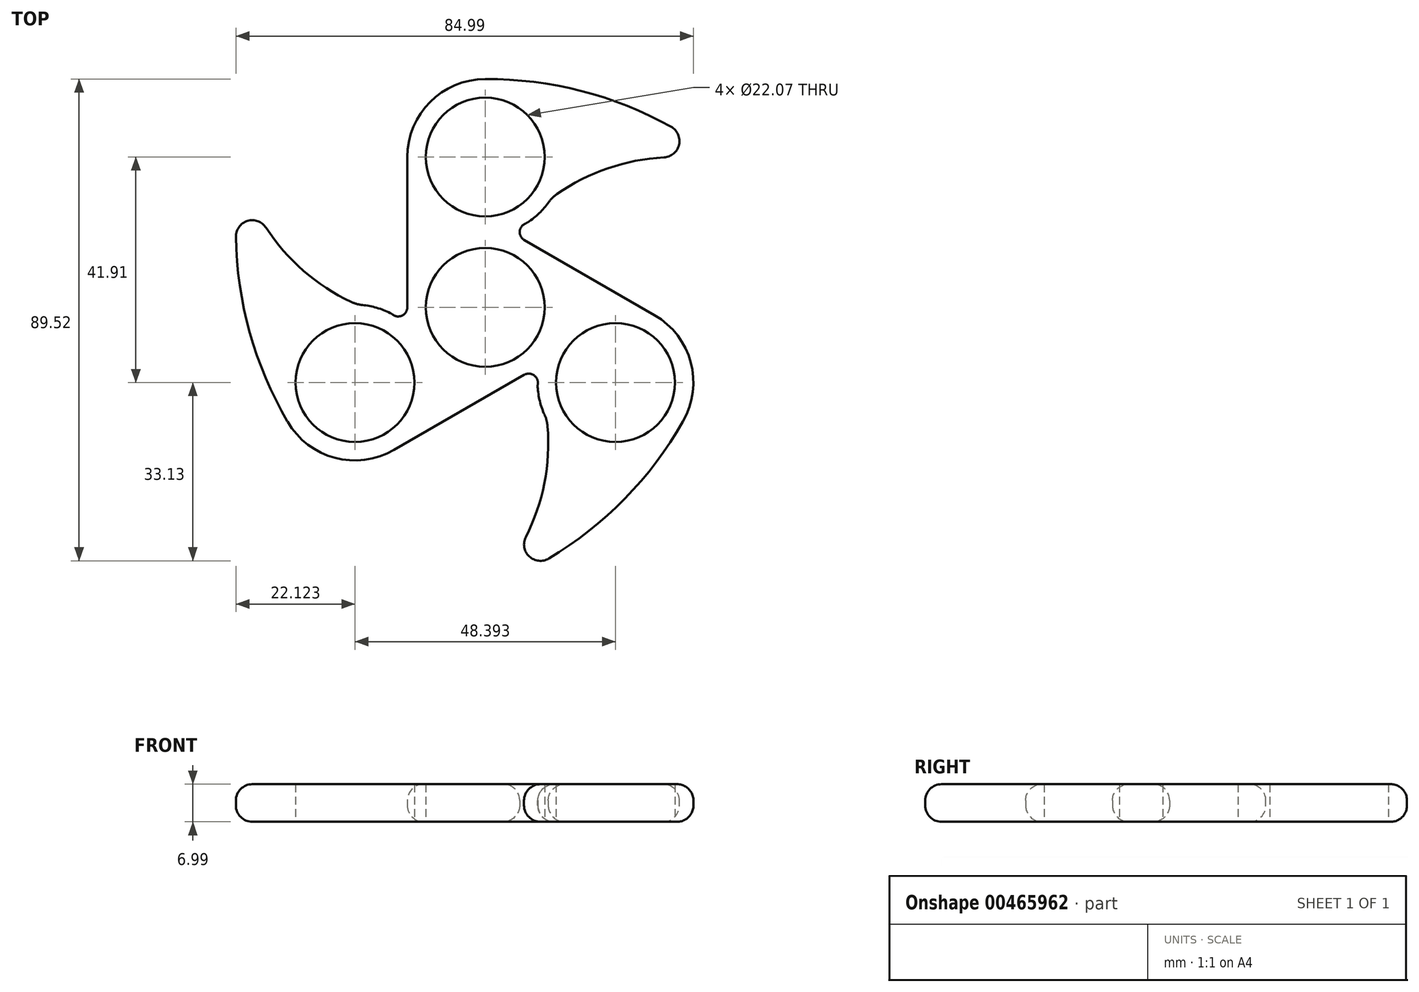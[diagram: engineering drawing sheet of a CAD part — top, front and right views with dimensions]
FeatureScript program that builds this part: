
annotation { "Feature Type Name" : "Feature", "Feature Type Description" : "" }
export const myFeature = defineFeature(function(context is Context, id is Id, definition is map)
    precondition{}
    {
        {
            var Q0;
            Q0=qCreatedBy(makeId("Top.planeOp"),FACE);
            var sketch = newSketch(context, id + "F0", { "sketchPlane" : qUnion([Q0])});
            skCircle(sketch, "E0", {"center": v(0, 0) * mm, "radius": 11.04 * mm});
            skCircle(sketch, "E1", {"center": v(0, 27.94) * mm, "radius": 11.04 * mm});
            skCircle(sketch, "E2.1.0", {"center": v(-24.2, -13.97) * mm, "radius": 11.04 * mm});
            skCircle(sketch, "E2.2.0", {"center": v(24.2, -13.97) * mm, "radius": 11.04 * mm});
            skCircle(sketch, "E3", {"center": v(0, 27.94) * mm, "radius": 12.7 * mm});
            skCircle(sketch, "E4", {"center": v(-24.2, -13.97) * mm, "radius": 12.7 * mm});
            skCircle(sketch, "E5", {"center": v(0, 0) * mm, "radius": 12.7 * mm});
            skCircle(sketch, "E6", {"center": v(24.2, -13.97) * mm, "radius": 12.7 * mm});
            skLineSegment(sketch, "E7", {"start": v(0, 27.94) * mm, "end": v(-12.7, 27.94) * mm});
            skLineSegment(sketch, "E8", {"start": v(0, 0) * mm, "end": v(-12.7, 0) * mm});
            skLineSegment(sketch, "E9", {"start": v(-14.47, 27.94) * mm, "end": v(-14.47, 0) * mm});
            skLineSegment(sketch, "E10.2.1", {"start": v(31.43, -1.43) * mm, "end": v(7.24, 12.54) * mm});
            skArc(sketch, "E11", {"start": v(11.78, 19.53) * mm, "mid": v(9.9, 17.37) * mm, "end": v(7.61, 15.63) * mm});
            skArc(sketch, "E12", {"start": v(7.61, 15.63) * mm, "mid": v(6.4, 14.2) * mm, "end": v(7.24, 12.54) * mm});
            skLineSegment(sketch, "E13.1.0", {"start": v(-16.96, -26.5) * mm, "end": v(7.24, -12.54) * mm});
            skArc(sketch, "E13.1.1", {"start": v(-16.96, -26.5) * mm, "mid": v(-38.67, -14.19) * mm, "end": v(-17.34, -1.22) * mm});
            skArc(sketch, "E13.1.2", {"start": v(-17.34, -1.22) * mm, "mid": v(-15.5, -1.56) * mm, "end": v(-14.47, 0) * mm});
            skArc(sketch, "E13.2.1", {"start": v(31.43, -1.43) * mm, "mid": v(31.62, -26.4) * mm, "end": v(9.73, -14.4) * mm});
            skArc(sketch, "E13.2.2", {"start": v(9.73, -14.4) * mm, "mid": v(9.1, -12.65) * mm, "end": v(7.24, -12.54) * mm});
            skLineSegment(sketch, "E14", {"start": v(0, 27.94) * mm, "end": v(0, 42.41) * mm});
            skArc(sketch, "E15", {"start": v(44.57, 26.77) * mm, "mid": v(23.64, 38.45) * mm, "end": v(0, 42.41) * mm});
            skArc(sketch, "E16", {"start": v(44.57, 26.77) * mm, "mid": v(28.33, 27.3) * mm, "end": v(13.33, 21.06) * mm});
            skPoint(sketch, "E17.newPointB", {"position": v(-14.47, 27.94) * mm});
            skArc(sketch, "E17.filletArc", {"start": v(13.33, 21.06) * mm, "mid": v(12.5, 20.36) * mm, "end": v(11.78, 19.53) * mm});
            skArc(sketch, "E18", {"start": v(0, 42.41) * mm, "mid": v(-10.24, 38.18) * mm, "end": v(-14.47, 27.94) * mm});
            skArc(sketch, "E19.1.0", {"start": v(-45.47, 25.21) * mm, "mid": v(-45.12, 1.25) * mm, "end": v(-36.73, -21.2) * mm});
            skArc(sketch, "E19.1.1", {"start": v(-45.47, 25.21) * mm, "mid": v(-37.8, 10.9) * mm, "end": v(-24.9, 1.02) * mm});
            skArc(sketch, "E19.1.2", {"start": v(-22.8, 0.44) * mm, "mid": v(-20, -0.12) * mm, "end": v(-17.34, -1.22) * mm});
            skArc(sketch, "E19.1.3", {"start": v(-24.9, 1.02) * mm, "mid": v(-23.88, 0.64) * mm, "end": v(-22.8, 0.44) * mm});
            skArc(sketch, "E19.2.0", {"start": v(0.9, -51.98) * mm, "mid": v(21.48, -39.7) * mm, "end": v(36.73, -21.2) * mm});
            skArc(sketch, "E19.2.1", {"start": v(0.9, -51.98) * mm, "mid": v(9.47, -38.18) * mm, "end": v(11.57, -22.08) * mm});
            skArc(sketch, "E19.2.2", {"start": v(11.02, -19.97) * mm, "mid": v(10.1, -17.25) * mm, "end": v(9.73, -14.4) * mm});
            skArc(sketch, "E19.2.3", {"start": v(11.57, -22.08) * mm, "mid": v(11.39, -21) * mm, "end": v(11.02, -19.97) * mm});
            skSolve(sketch);
        }
        {
            var Q0;
            {var subQ2=sQuery(id+"F0.wireOp",EDGE,"E19.2.0");Q0=makeQuery(id+"F0.imprint","IMPRINT",FACE,{"disambiguationData":[TD([[makeQuery(id+"F0.imprint","IMPRINT",EDGE,{"derivedFrom":subQ2}),1.0]])]});}
            var Q1;
            Q1=makeQuery(id+"F0.imprint","IMPRINT",FACE,{"disambiguationData":[TD([[makeQuery(id+"F0.imprint","IMPRINT",EDGE,{"derivedFrom":sQuery(id+"F0.wireOp",EDGE,"E4")}),-1.0]])]});
            var Q2;
            Q2=makeQuery(id+"F0.imprint","IMPRINT",FACE,{"disambiguationData":[TD([[makeQuery(id+"F0.imprint","IMPRINT",EDGE,{"derivedFrom":sQuery(id+"F0.wireOp",EDGE,"E2.2.0")}),-1.0]])]});
            var Q3;
            {var subQ0=sQuery(id+"F0.wireOp",EDGE,"E7");var subQ1=sQuery(id+"F0.wireOp",EDGE,"E1");var subQ2=makeQuery(id+"F0.imprint","INTERSECT",VERTEX,{"derivedFrom":[subQ1,subQ0]});Q3=makeQuery(id+"F0.imprint","IMPRINT",FACE,{"disambiguationData":[TD([[makeQuery(id+"F0.imprint","IMPRINT",EDGE,{"disambiguationData":[TD([[subQ2,1.0]])],"derivedFrom":subQ1}),-1.0]])]});}
            var Q4;
            {var subQ0=sQuery(id+"F0.wireOp",EDGE,"E7");var subQ1=sQuery(id+"F0.wireOp",EDGE,"E1");var subQ2=makeQuery(id+"F0.imprint","INTERSECT",VERTEX,{"derivedFrom":[subQ1,subQ0]});Q4=makeQuery(id+"F0.imprint","IMPRINT",FACE,{"disambiguationData":[TD([[makeQuery(id+"F0.imprint","IMPRINT",EDGE,{"disambiguationData":[TD([[subQ2,-1.0]])],"derivedFrom":subQ1}),-1.0]])]});}
            var Q5;
            Q5=makeQuery(id+"F0.imprint","IMPRINT",FACE,{"disambiguationData":[TD([[makeQuery(id+"F0.imprint","IMPRINT",EDGE,{"derivedFrom":sQuery(id+"F0.wireOp",EDGE,"E0")}),-1.0]])]});
            var Q6;
            Q6=makeQuery(id+"F0.imprint","IMPRINT",FACE,{"disambiguationData":[TD([[makeQuery(id+"F0.imprint","IMPRINT",EDGE,{"derivedFrom":sQuery(id+"F0.wireOp",EDGE,"E2.1.0")}),-1.0]])]});
            var Q7;
            {var subQ2=sQuery(id+"F0.wireOp",EDGE,"E19.1.0");Q7=makeQuery(id+"F0.imprint","IMPRINT",FACE,{"disambiguationData":[TD([[makeQuery(id+"F0.imprint","IMPRINT",EDGE,{"derivedFrom":subQ2}),1.0]])]});}
            extrude(context, id + "F1", {"entities" : qUnion([Q0, Q1, Q2, Q3, Q4, Q5, Q6, Q7]), "depth" : 7 * mm});
        }
        {
            var Q0;
            Q0=makeQuery(id+"F1.opExtrude","SWEPT_FACE",FACE,{"disambiguationData":[OSD([sQuery(id+"F0.wireOp",EDGE,"E19.2.1")])]});
            var Q1;
            Q1=makeQuery(id+"F1.opExtrude","SWEPT_FACE",FACE,{"disambiguationData":[OSD([sQuery(id+"F0.wireOp",EDGE,"E19.2.3")])]});
            var Q2;
            Q2=makeQuery(id+"F1.opExtrude","SWEPT_FACE",FACE,{"disambiguationData":[OSD([sQuery(id+"F0.wireOp",EDGE,"E19.2.2")])]});
            var Q3;
            Q3=makeQuery(id+"F1.opExtrude","SWEPT_FACE",FACE,{"disambiguationData":[OSD([sQuery(id+"F0.wireOp",EDGE,"E13.2.2")])]});
            var Q4;
            Q4=makeQuery(id+"F1.opExtrude","SWEPT_FACE",FACE,{"disambiguationData":[OSD([sQuery(id+"F0.wireOp",EDGE,"E13.1.0")])]});
            var Q5;
            Q5=makeQuery(id+"F1.opExtrude","SWEPT_FACE",FACE,{"disambiguationData":[OSD([sQuery(id+"F0.wireOp",EDGE,"E13.1.1")])]});
            var Q6;
            Q6=makeQuery(id+"F1.opExtrude","SWEPT_FACE",FACE,{"disambiguationData":[OSD([sQuery(id+"F0.wireOp",EDGE,"E19.1.0")])]});
            var Q7;
            Q7=makeQuery(id+"F1.opExtrude","SWEPT_FACE",FACE,{"disambiguationData":[OSD([sQuery(id+"F0.wireOp",EDGE,"E19.1.1")])]});
            var Q8;
            Q8=makeQuery(id+"F1.opExtrude","SWEPT_FACE",FACE,{"disambiguationData":[OSD([sQuery(id+"F0.wireOp",EDGE,"E19.1.3")])]});
            var Q9;
            Q9=makeQuery(id+"F1.opExtrude","SWEPT_FACE",FACE,{"disambiguationData":[OSD([sQuery(id+"F0.wireOp",EDGE,"E19.1.2")])]});
            var Q10;
            Q10=makeQuery(id+"F1.opExtrude","SWEPT_FACE",FACE,{"disambiguationData":[OSD([sQuery(id+"F0.wireOp",EDGE,"E13.1.2")])]});
            var Q11;
            Q11=makeQuery(id+"F1.opExtrude","SWEPT_FACE",FACE,{"disambiguationData":[OSD([sQuery(id+"F0.wireOp",EDGE,"E9")])]});
            var Q12;
            Q12=makeQuery(id+"F1.opExtrude","SWEPT_FACE",FACE,{"disambiguationData":[OSD([sQuery(id+"F0.wireOp",EDGE,"E18")])]});
            var Q13;
            Q13=makeQuery(id+"F1.opExtrude","SWEPT_FACE",FACE,{"disambiguationData":[OSD([sQuery(id+"F0.wireOp",EDGE,"E15")])]});
            var Q14;
            Q14=makeQuery(id+"F1.opExtrude","SWEPT_FACE",FACE,{"disambiguationData":[OSD([sQuery(id+"F0.wireOp",EDGE,"E11")])]});
            var Q15;
            Q15=makeQuery(id+"F1.opExtrude","SWEPT_EDGE",EDGE,{"disambiguationData":[OSD([sQuery(id+"F0.wireOp",EDGE,"E11"),sQuery(id+"F0.wireOp",EDGE,"E17.filletArc")])]});
            var Q16;
            Q16=makeQuery(id+"F1.opExtrude","SWEPT_FACE",FACE,{"disambiguationData":[OSD([sQuery(id+"F0.wireOp",EDGE,"E12")])]});
            var Q17;
            Q17=makeQuery(id+"F1.opExtrude","SWEPT_FACE",FACE,{"disambiguationData":[OSD([sQuery(id+"F0.wireOp",EDGE,"E10.2.1")])]});
            var Q18;
            Q18=makeQuery(id+"F1.opExtrude","CAP_EDGE",EDGE,{"disambiguationData":[OSD([sQuery(id+"F0.wireOp",EDGE,"E16")])],"isStart":true});
            var Q19;
            Q19=makeQuery(id+"F1.opExtrude","SWEPT_EDGE",EDGE,{"disambiguationData":[OSD([sQuery(id+"F0.wireOp",EDGE,"E16"),sQuery(id+"F0.wireOp",EDGE,"E17.filletArc")])]});
            var Q20;
            Q20=makeQuery(id+"F1.opExtrude","SWEPT_FACE",FACE,{"disambiguationData":[OSD([sQuery(id+"F0.wireOp",EDGE,"E17.filletArc")])]});
            var Q21;
            Q21=makeQuery(id+"F1.opExtrude","SWEPT_FACE",FACE,{"disambiguationData":[OSD([sQuery(id+"F0.wireOp",EDGE,"E13.2.1")])]});
            var Q22;
            Q22=makeQuery(id+"F1.opExtrude","SWEPT_FACE",FACE,{"disambiguationData":[OSD([sQuery(id+"F0.wireOp",EDGE,"E19.2.0")])]});
            fillet(context, id + "F2", {"entities" : qUnion([Q0, Q1, Q2, Q3, Q4, Q5, Q6, Q7, Q8, Q9, Q10, Q11, Q12, Q13, Q14, Q15, Q16, Q17, Q18, Q19, Q20, Q21, Q22]), "radius" : 3.05 * mm, "tangentPropagation" : true, "allowEdgeOverflow" : false});
        }
    });
